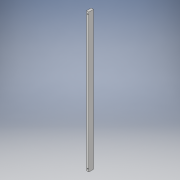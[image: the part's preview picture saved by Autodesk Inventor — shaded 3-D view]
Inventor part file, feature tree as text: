
AUTODESK INVENTOR PART (.ipt)
format: ipt  version: 2017 (Build 210142000, 142)  size: 106,496 bytes
history: native  units: in
note: dims shown in document units (in); Inventor stores cm internally (conversion verified against a paired STEP export)
features: sketch x2, extrude x1, hole x1
ambient origin geometry x8: Origin, YZ Plane, XZ Plane, XY Plane, X Axis, Y Axis, Z Axis, Center Point
bodies: Solid1 (feature_tree)
feature tree (4):
  extrude  "Extrusion1"  Depth=14.75in
  hole  "Hole1"  [1 undecoded]
  sketch  "Sketch1"  dims[d0=0.25in d1=14.75in]
  sketch  "Sketch2"  dims[d2=0.5in d3=0.0in d4=0.25in d5=0.14in d6=0.25in d7=0.14in d10=0.104in d11=0.5in d12=0.375in d13=0.25in d14=0.5635in d15=0.5in d16=0.8108in]
note: 1 required parameter value undecoded (feature->parameter linkage not recoverable at this tier; creation-order binding heuristic only, values carry confidence <= 0.55)
